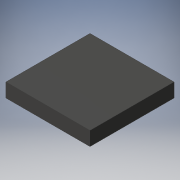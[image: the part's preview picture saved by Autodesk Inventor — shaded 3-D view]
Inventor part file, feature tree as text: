
AUTODESK INVENTOR PART (.ipt)
format: ipt  version: 2016 (Build 200138000, 138)  size: 84,992 bytes
history: native  units: in
note: dims shown in document units (in); Inventor stores cm internally (conversion verified against a paired STEP export)
features: extrude x1, sketch x1
ambient origin geometry x8: Origin, YZ Plane, XZ Plane, XY Plane, X Axis, Y Axis, Z Axis, Center Point
bodies: Solid1 (feature_tree)
feature tree (2):
  extrude  "Extrusion1"  Depth=12.0in
  sketch  "Sketch1"  dims[d0=12.0in d1=12.0in d2=2.0in d3=0.0in]
